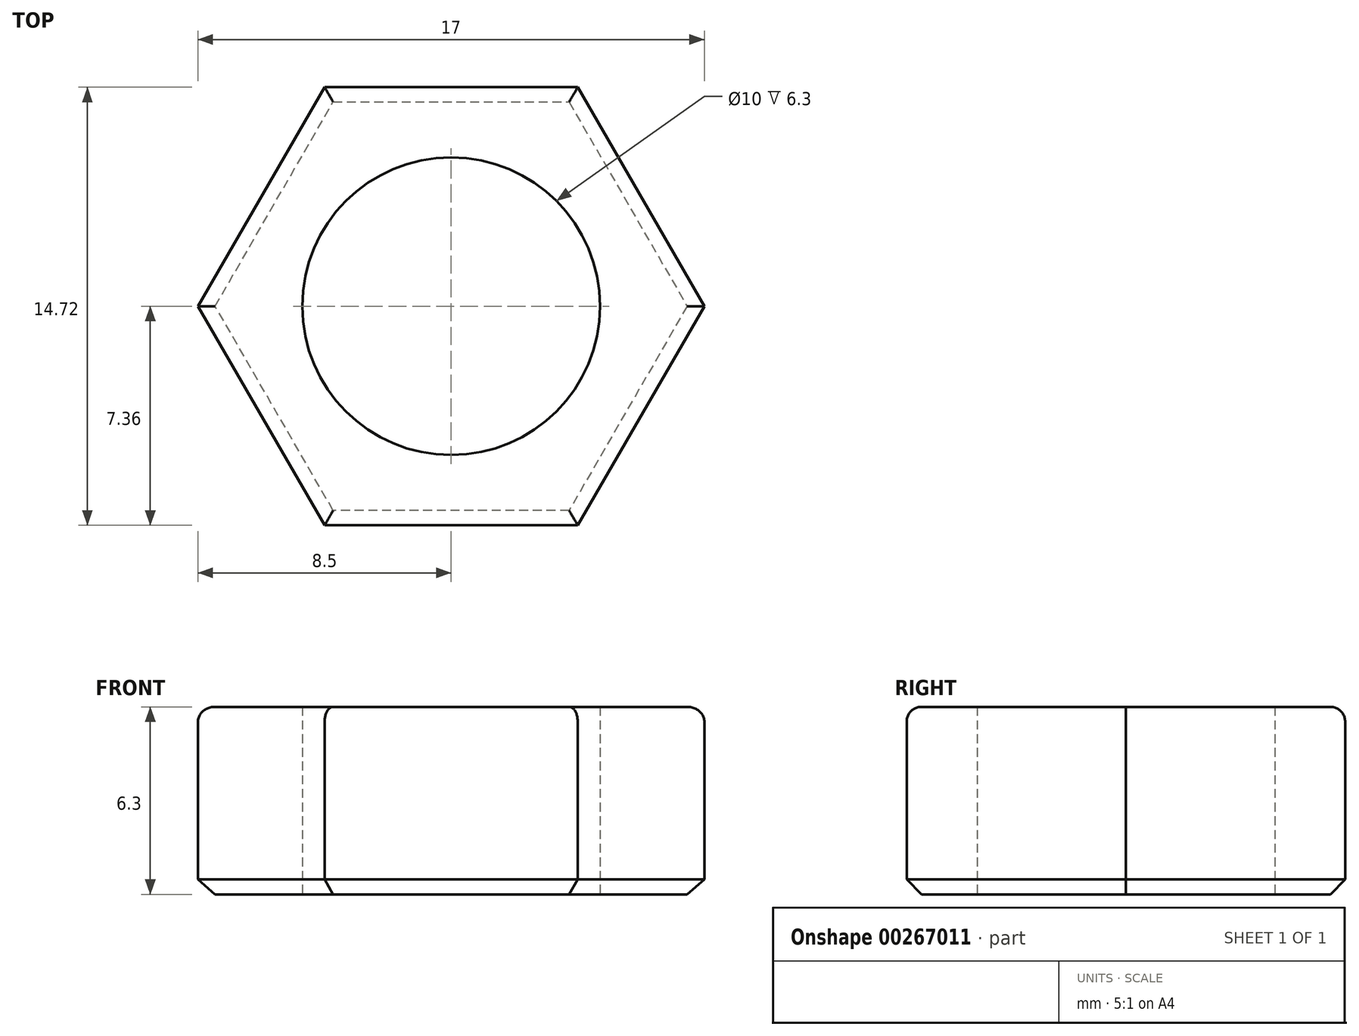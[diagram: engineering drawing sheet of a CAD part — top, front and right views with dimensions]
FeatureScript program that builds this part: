
annotation { "Feature Type Name" : "Feature", "Feature Type Description" : "" }
export const myFeature = defineFeature(function(context is Context, id is Id, definition is map)
    precondition{}
    {
        {
            var Q0;
            Q0=qCreatedBy(makeId("Top.planeOp"),FACE);
            var sketch = newSketch(context, id + "F0", { "sketchPlane" : qUnion([Q0])});
            skCircle(sketch, "E0.cCircle", {"center": v(0, 0) * mm, "radius": 8.5 * mm, "construction": true});
            skLineSegment(sketch, "E0.0", {"start": v(8.5, 0) * mm, "end": v(4.25, -7.36) * mm});
            skLineSegment(sketch, "E0.1", {"start": v(4.25, -7.36) * mm, "end": v(-4.25, -7.36) * mm});
            skLineSegment(sketch, "E0.2", {"start": v(-4.25, -7.36) * mm, "end": v(-8.5, 0) * mm});
            skLineSegment(sketch, "E0.3", {"start": v(-8.5, 0) * mm, "end": v(-4.25, 7.36) * mm});
            skLineSegment(sketch, "E0.4", {"start": v(-4.25, 7.36) * mm, "end": v(4.25, 7.36) * mm});
            skLineSegment(sketch, "E0.5", {"start": v(4.25, 7.36) * mm, "end": v(8.5, 0) * mm});
            skSolve(sketch);
        }
        {
            var Q0;
            Q0=makeQuery(id+"F0.imprint","IMPRINT",FACE,{"disambiguationData":[TD([[makeQuery(id+"F0.imprint","IMPRINT",EDGE,{"derivedFrom":sQuery(id+"F0.wireOp",EDGE,"E0.0")}),-1.0]])]});
            extrude(context, id + "F1", {"entities" : qUnion([Q0]), "depth" : 6.3 * mm});
        }
        {
            var Q0;
            Q0=qCreatedBy(makeId("Top.planeOp"),FACE);
            var sketch = newSketch(context, id + "F2", { "sketchPlane" : qUnion([Q0])});
            skCircle(sketch, "E1", {"center": v(0, 0) * mm, "radius": 4.85 * mm});
            skSolve(sketch);
        }
        {
            var Q0;
            Q0=makeQuery(id+"F1.opExtrude","CAP_EDGE",EDGE,{"disambiguationData":[OSD([sQuery(id+"F0.wireOp",EDGE,"E0.1")])],"isStart":false});
            var Q1;
            Q1=makeQuery(id+"F1.opExtrude","CAP_EDGE",EDGE,{"disambiguationData":[OSD([sQuery(id+"F0.wireOp",EDGE,"E0.0")])],"isStart":false});
            var Q2;
            Q2=makeQuery(id+"F1.opExtrude","CAP_EDGE",EDGE,{"disambiguationData":[OSD([sQuery(id+"F0.wireOp",EDGE,"E0.5")])],"isStart":false});
            var Q3;
            Q3=makeQuery(id+"F1.opExtrude","CAP_EDGE",EDGE,{"disambiguationData":[OSD([sQuery(id+"F0.wireOp",EDGE,"E0.4")])],"isStart":false});
            var Q4;
            Q4=makeQuery(id+"F1.opExtrude","CAP_EDGE",EDGE,{"disambiguationData":[OSD([sQuery(id+"F0.wireOp",EDGE,"E0.3")])],"isStart":false});
            var Q5;
            Q5=makeQuery(id+"F1.opExtrude","CAP_EDGE",EDGE,{"disambiguationData":[OSD([sQuery(id+"F0.wireOp",EDGE,"E0.2")])],"isStart":false});
            fillet(context, id + "F3", {"entities" : qUnion([Q0, Q1, Q2, Q3, Q4, Q5]), "radius" : 0.5 * mm, "tangentPropagation" : true, "allowEdgeOverflow" : false});
        }
        {
            var Q0;
            Q0=sQuery(id+"F2.wireOp",VERTEX,"E1.center");
            var Q1;
            Q1=makeQuery(id+"F1.opExtrude","SWEPT_BODY",BODY,{"disambiguationData":[OSD([sQuery(id+"F0.wireOp",EDGE,"E0.0"),sQuery(id+"F0.wireOp",EDGE,"E0.1"),sQuery(id+"F0.wireOp",EDGE,"E0.2"),sQuery(id+"F0.wireOp",EDGE,"E0.3"),sQuery(id+"F0.wireOp",EDGE,"E0.4"),sQuery(id+"F0.wireOp",EDGE,"E0.5")])]});
            hole(context, id + "F4", {"style" : HoleStyle.SIMPLE, "endStyle" : HoleEndStyle.THROUGH, "oppositeDirection" : true, "holeDiameter" : 10 * mm, "tappedDepth" : 12 * mm, "tapClearance" : 3, "locations" : qUnion([Q0]), "scope" : qUnion([Q1])});
        }
        {
            var Q0;
            Q0=makeQuery(id+"F1.opExtrude","CAP_EDGE",EDGE,{"disambiguationData":[OSD([sQuery(id+"F0.wireOp",EDGE,"E0.3")])],"isStart":true});
            var Q1;
            Q1=makeQuery(id+"F1.opExtrude","CAP_EDGE",EDGE,{"disambiguationData":[OSD([sQuery(id+"F0.wireOp",EDGE,"E0.4")])],"isStart":true});
            var Q2;
            Q2=makeQuery(id+"F1.opExtrude","CAP_EDGE",EDGE,{"disambiguationData":[OSD([sQuery(id+"F0.wireOp",EDGE,"E0.2")])],"isStart":true});
            var Q3;
            Q3=makeQuery(id+"F1.opExtrude","CAP_EDGE",EDGE,{"disambiguationData":[OSD([sQuery(id+"F0.wireOp",EDGE,"E0.1")])],"isStart":true});
            var Q4;
            Q4=makeQuery(id+"F1.opExtrude","CAP_EDGE",EDGE,{"disambiguationData":[OSD([sQuery(id+"F0.wireOp",EDGE,"E0.0")])],"isStart":true});
            var Q5;
            Q5=makeQuery(id+"F1.opExtrude","CAP_EDGE",EDGE,{"disambiguationData":[OSD([sQuery(id+"F0.wireOp",EDGE,"E0.5")])],"isStart":true});
            chamfer(context, id + "F5", {"entities" : qUnion([Q0, Q1, Q2, Q3, Q4, Q5]), "width" : 0.5 * mm, "tangentPropagation" : true});
        }
    });
